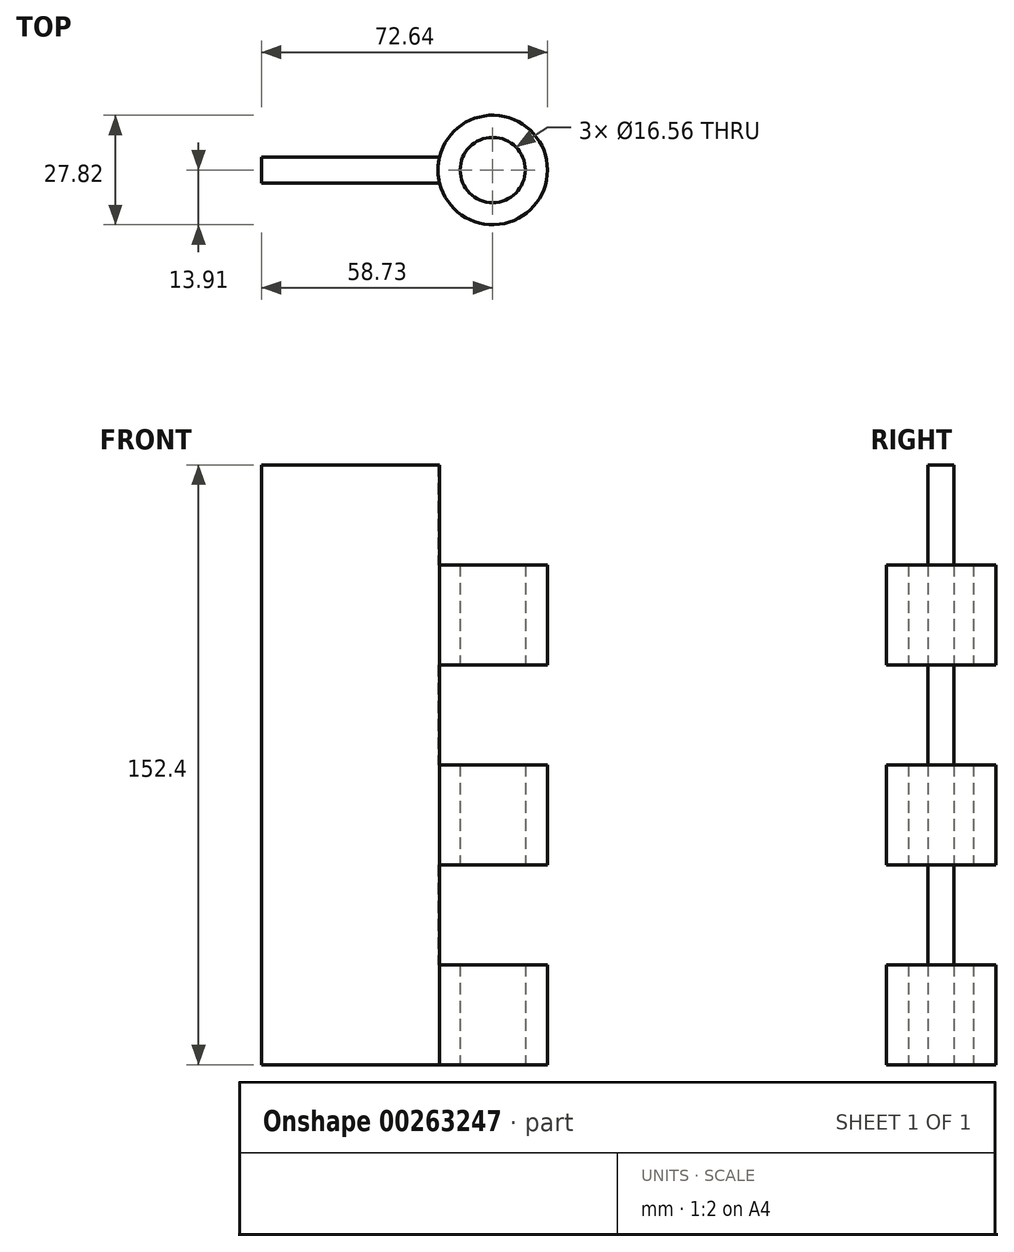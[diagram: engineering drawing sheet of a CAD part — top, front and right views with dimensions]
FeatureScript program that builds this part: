
annotation { "Feature Type Name" : "Feature", "Feature Type Description" : "" }
export const myFeature = defineFeature(function(context is Context, id is Id, definition is map)
    precondition{}
    {
        {
            var Q0;
            Q0=qCreatedBy(makeId("Top.planeOp"),FACE);
            var sketch = newSketch(context, id + "F0", { "sketchPlane" : qUnion([Q0])});
            skPoint(sketch, "E0.middle", {"position": v(0, 0) * mm});
            skCircle(sketch, "E1", {"center": v(0, 0) * mm, "radius": 8.28 * mm});
            skLineSegment(sketch, "E2", {"start": v(-13.5, 3.32) * mm, "end": v(-58.73, 3.32) * mm});
            skLineSegment(sketch, "E3.MirrorCS", {"start": v(-13.5, -3.32) * mm, "end": v(-58.73, -3.32) * mm});
            skLineSegment(sketch, "E4", {"start": v(-58.73, 3.32) * mm, "end": v(-58.73, -3.32) * mm});
            skCircle(sketch, "E5", {"center": v(0, 0) * mm, "radius": 13.9 * mm});
            skSolve(sketch);
        }
        {
            var Q0;
            {var subQ0=sQuery(id+"F0.wireOp",EDGE,"E2");Q0=makeQuery(id+"F0.imprint","IMPRINT",FACE,{"disambiguationData":[TD([[makeQuery(id+"F0.imprint","IMPRINT",EDGE,{"derivedFrom":subQ0}),1.0]])]});}
            extrude(context, id + "F1", {"entities" : qUnion([Q0]), "depth" : 152.4 * mm});
        }
        {
            var Q0;
            Q0=makeQuery(id+"F0.imprint","IMPRINT",FACE,{"disambiguationData":[TD([[makeQuery(id+"F0.imprint","IMPRINT",EDGE,{"derivedFrom":sQuery(id+"F0.wireOp",EDGE,"E1")}),-1.0]])]});
            extrude(context, id + "F2", {"entities" : qUnion([Q0]), "operationType" : NewBodyOperationType.ADD, "depth" : 25.4 * mm});
        }
        {
            var Q0;
            Q0=qCreatedBy(makeId("Top.planeOp"),FACE);
            cPlane(context, id + "F3", {"entities" : qUnion([Q0]), "cplaneType" : CPlaneType.OFFSET, "offset" : 50.8 * mm, "width" : 152.4 * mm, "height" : 152.4 * mm});
        }
        {
            var Q0;
            Q0=qCreatedBy(id+"F3.planeOp",FACE);
            cPlane(context, id + "F4", {"entities" : qUnion([Q0]), "cplaneType" : CPlaneType.OFFSET, "offset" : 50.8 * mm, "width" : 152.4 * mm, "height" : 152.4 * mm});
        }
        {
            var Q0;
            Q0=qCreatedBy(id+"F3.planeOp",FACE);
            var sketch = newSketch(context, id + "F5", { "sketchPlane" : qUnion([Q0])});
            skArc(sketch, "E6.0.0", {"start": v(-13.5, 3.32) * mm, "mid": v(-13.9, 0) * mm, "end": v(-13.5, -3.32) * mm});
            skArc(sketch, "E6.0.1", {"start": v(-13.5, -3.32) * mm, "mid": v(13.9, 0) * mm, "end": v(-13.5, 3.32) * mm});
            skCircle(sketch, "E7.0", {"center": v(0, 0) * mm, "radius": 8.28 * mm});
            skSolve(sketch);
        }
        {
            var Q0;
            Q0=makeQuery(id+"F5.imprint","IMPRINT",FACE,{"disambiguationData":[TD([[makeQuery(id+"F5.imprint","IMPRINT",EDGE,{"derivedFrom":sQuery(id+"F5.wireOp",EDGE,"E6.0.0")}),1.0]])]});
            extrude(context, id + "F6", {"entities" : qUnion([Q0]), "operationType" : NewBodyOperationType.ADD, "depth" : 25.4 * mm});
        }
        {
            var Q0;
            Q0=qCreatedBy(id+"F4.planeOp",FACE);
            var sketch = newSketch(context, id + "F7", { "sketchPlane" : qUnion([Q0])});
            skArc(sketch, "E8.0.0", {"start": v(-13.5, 3.32) * mm, "mid": v(-13.9, 0) * mm, "end": v(-13.5, -3.32) * mm});
            skArc(sketch, "E8.0.1", {"start": v(-13.5, -3.32) * mm, "mid": v(13.9, 0) * mm, "end": v(-13.5, 3.32) * mm});
            skCircle(sketch, "E9.0", {"center": v(0, 0) * mm, "radius": 8.28 * mm});
            skSolve(sketch);
        }
        {
            var Q0;
            Q0=makeQuery(id+"F7.imprint","IMPRINT",FACE,{"disambiguationData":[TD([[makeQuery(id+"F7.imprint","IMPRINT",EDGE,{"derivedFrom":sQuery(id+"F7.wireOp",EDGE,"E8.0.0")}),1.0]])]});
            extrude(context, id + "F8", {"entities" : qUnion([Q0]), "operationType" : NewBodyOperationType.ADD, "depth" : 25.4 * mm});
        }
    });
